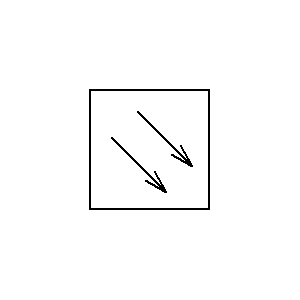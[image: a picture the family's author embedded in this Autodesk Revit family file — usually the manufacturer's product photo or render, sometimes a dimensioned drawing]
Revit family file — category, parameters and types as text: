
# Revit family: Gira_114502
name_source: partatom
category: Electrical Fixtures
revit_build: Autodesk Revit 2017 (Build: 20160225_1515(x64)
units: mm (PartAtom-declared; Revit-internal decimal feet)

## family parameters
Cut with Voids When Loaded = No
Host = Face
Maintain Annotation Orientation = No
Part Type = Normal
Room Calculation Point = No
Round Connector Dimension = Use Diameter
Shared = No

## types (1)
- SAD Basic Q Smoke alarm device p.white
    Available = No
    BIM (1) = https://media.stage.bim.site
    Backup battery included = None
    Cable entry = Bottom side
    Category = Fire detector
    Colour = White
    Current supply primary = Battery/accumulator
    Data sheet (1) = https://katalog.gira.de
    Default Elevation = 1219 mm
    Degree of protection (IP) = IP42
    Description = SAD Basic Q SAD PW,Smoke alarm device Basic Q,,pure white glossy,Increased quality criteria and technical advancements in smoke alarm devices are indicated on the market with the new Q test mark. The new Q-Label is an autonomous, manufacturer-independent quality mark for high-quality smoke alarm devices which undergo special testing for long-term use. The latest generation of Gira smoke alarm devices fulfil the criteria of the new Q-Label quality mark. The smoke alarm devices operate based on the photoelectric scattered light principle without radioactive particles. The smoke alarm devices detect smoke accumulation early and emit a warning signal before the concentration of smoke can become hazardous to people. Alerting occurs via a loud pulsing alarm tone and a flashing LED.,,Features:,- Use in private residential units or similarly inhabited areas only in accordance with DIN 14676.,Q-Label:,- Tested durability and reduction of deceptive alarms.,- Increased stability, e.g. against external factors.,- Permanently installed battery with a service life of up to 10 years.,- Design A as per DIN EN 14604.,- KRIWAN approval.,- Integrated function button for function test.,- Fault indication.,- Weak battery indication.
    Diameter = 0.125
    Explosion-tested version = No
    GTIN = 4010337013525
    HAN = 114502
    Height = 0.0385
    HeinzeBIM = https://bimportal.heinze.de
    Loudness = 85
    Manufacturer = Gira
    Manufacturer URL = https://www.gira.de
    Mounting method = Surface mounting
    Name = SAD Basic Q Smoke alarm device p.white
    Networkable via cable = No
    Networkable via radio optional = No
    Operating principle = Optic
    Smoke switcher = No
    Standalone = Yes
    Standard networkable via radio = No
    Suitable for duct mounting = No
    Supply voltage = 9 - 9
    Type of test-/pause button = Test button
    URL = http://katalog.gira.de
    VdS accepted = No
    Voltage type of supply voltage = Ac
    With backup battery = No
    With orientation lighting = No
    With socket = Yes
    With voltage indication = No

## geometry (parser evidence)
native form markers: Sweep x3
no freeform markers — native parametric forms only
